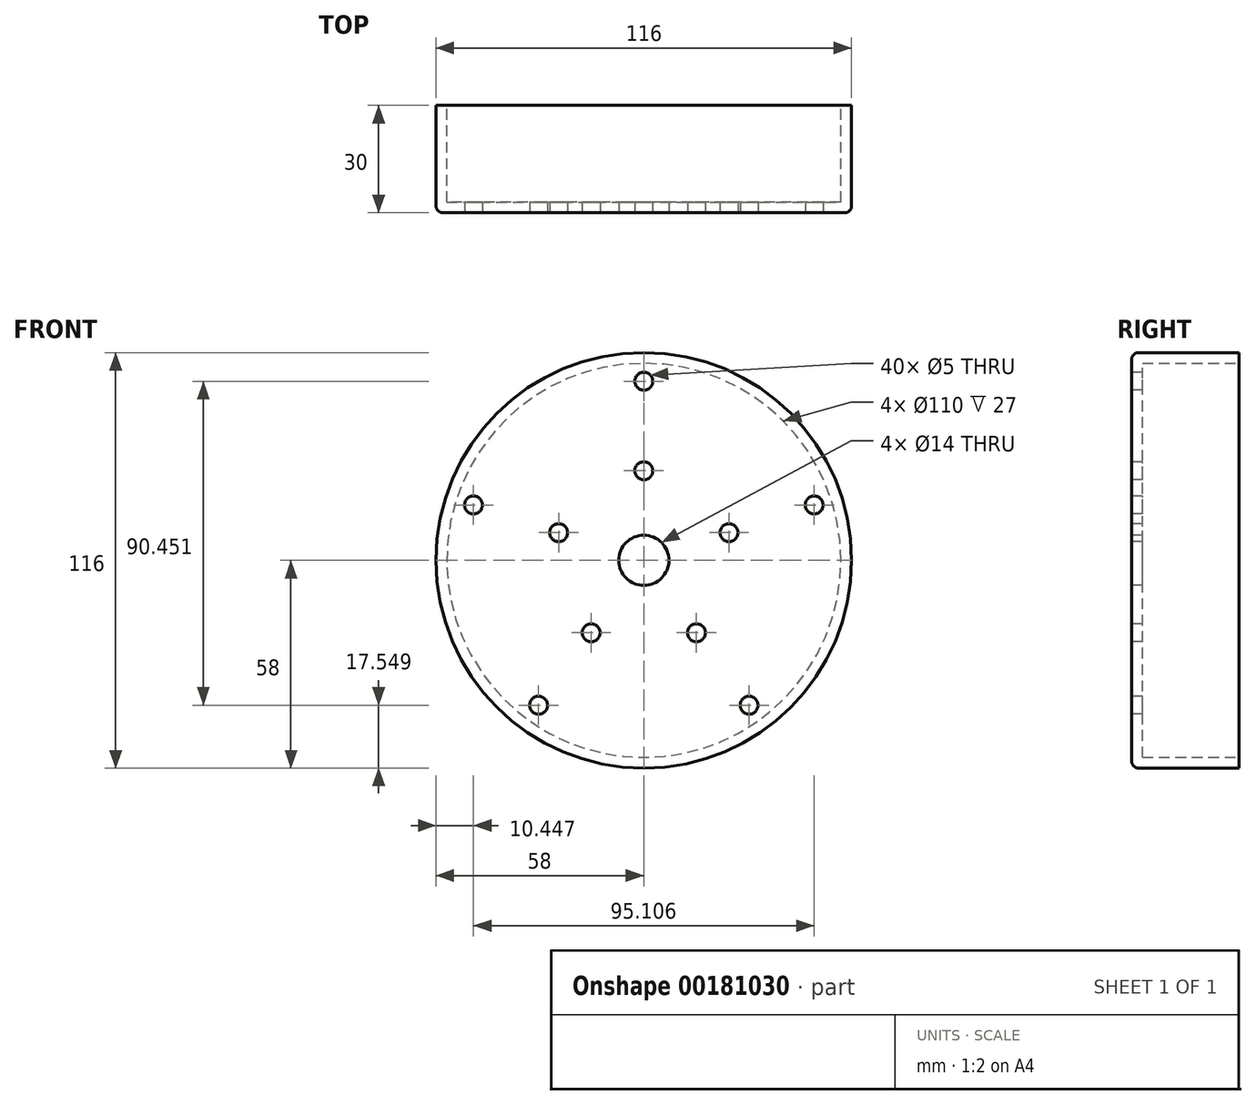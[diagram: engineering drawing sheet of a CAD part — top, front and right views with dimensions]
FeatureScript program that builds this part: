
annotation { "Feature Type Name" : "Feature", "Feature Type Description" : "" }
export const myFeature = defineFeature(function(context is Context, id is Id, definition is map)
    precondition{}
    {
        {
            var Q0;
            Q0=qCreatedBy(makeId("Front.planeOp"),FACE);
            var sketch = newSketch(context, id + "F0", { "sketchPlane" : qUnion([Q0])});
            skCircle(sketch, "E0", {"center": v(0, 0) * mm, "radius": 58 * mm});
            skSolve(sketch);
        }
        {
            var Q0;
            Q0=qSketchRegion(id+"F0",true);
            extrude(context, id + "F1", {"entities" : qUnion([Q0]), "depth" : 30 * mm});
        }
        {
            var Q0;
            Q0=makeQuery(id+"F1.opExtrude","CAP_FACE",FACE,{"disambiguationData":[OSD([sQuery(id+"F0.wireOp",EDGE,"E0")])],"isStart":true});
            shell(context, id + "F2", {"entities" : qUnion([Q0]), "thickness" : 3 * mm});
        }
        {
            var Q0;
            Q0=makeQuery(id+"F1.opExtrude","CAP_EDGE",EDGE,{"disambiguationData":[OSD([sQuery(id+"F0.wireOp",EDGE,"E0")])],"isStart":false});
            fillet(context, id + "F3", {"entities" : qUnion([Q0]), "radius" : 2 * mm, "tangentPropagation" : true, "allowEdgeOverflow" : false});
        }
        {
            var Q0;
            Q0=makeQuery(id+"F1.opExtrude","CAP_FACE",FACE,{"disambiguationData":[OSD([sQuery(id+"F0.wireOp",EDGE,"E0")])],"isStart":false});
            var sketch = newSketch(context, id + "F4", { "sketchPlane" : qUnion([Q0])});
            skPoint(sketch, "E1", {"position": v(0, 0) * mm});
            skSolve(sketch);
        }
        {
            var Q0;
            Q0=sQuery(id+"F4.wireOp",VERTEX,"E1");
            var Q1;
            Q1=makeQuery(id+"F1.opExtrude","SWEPT_BODY",BODY,{"disambiguationData":[OSD([sQuery(id+"F0.wireOp",EDGE,"E0")])]});
            hole(context, id + "F5", {"style" : HoleStyle.SIMPLE, "endStyle" : HoleEndStyle.THROUGH, "holeDiameter" : 14 * mm, "locations" : qUnion([Q0]), "scope" : qUnion([Q1]), "isTappedThrough" : true});
        }
        {
            var Q0;
            Q0=makeQuery(id+"F1.opExtrude","CAP_FACE",FACE,{"disambiguationData":[OSD([sQuery(id+"F0.wireOp",EDGE,"E0")])],"isStart":false});
            var sketch = newSketch(context, id + "F6", { "sketchPlane" : qUnion([Q0])});
            skPoint(sketch, "E2", {"position": v(0, 25) * mm});
            skPoint(sketch, "E3", {"position": v(0, 50) * mm});
            skPoint(sketch, "E4.1.0", {"position": v(-47.55, 15.45) * mm});
            skPoint(sketch, "E4.1.1", {"position": v(-23.78, 7.73) * mm});
            skPoint(sketch, "E4.2.0", {"position": v(-29.39, -40.45) * mm});
            skPoint(sketch, "E4.2.1", {"position": v(-14.7, -20.23) * mm});
            skPoint(sketch, "E4.3.0", {"position": v(29.39, -40.45) * mm});
            skPoint(sketch, "E4.3.1", {"position": v(14.7, -20.23) * mm});
            skPoint(sketch, "E4.4.0", {"position": v(47.55, 15.45) * mm});
            skPoint(sketch, "E4.4.1", {"position": v(23.78, 7.73) * mm});
            skPoint(sketch, "E4.center", {"position": v(0, 0) * mm});
            skSolve(sketch);
        }
        {
            var Q0;
            Q0=sQuery(id+"F6.wireOp",VERTEX,"E2");
            var Q1;
            Q1=sQuery(id+"F6.wireOp",VERTEX,"E3");
            var Q2;
            Q2=sQuery(id+"F6.wireOp",VERTEX,"E4.1.1");
            var Q3;
            Q3=sQuery(id+"F6.wireOp",VERTEX,"E4.1.0");
            var Q4;
            Q4=sQuery(id+"F6.wireOp",VERTEX,"E4.2.0");
            var Q5;
            Q5=sQuery(id+"F6.wireOp",VERTEX,"E4.2.1");
            var Q6;
            Q6=sQuery(id+"F6.wireOp",VERTEX,"E4.3.1");
            var Q7;
            Q7=sQuery(id+"F6.wireOp",VERTEX,"E4.3.0");
            var Q8;
            Q8=sQuery(id+"F6.wireOp",VERTEX,"E4.4.1");
            var Q9;
            Q9=sQuery(id+"F6.wireOp",VERTEX,"E4.4.0");
            var Q10;
            Q10=makeQuery(id+"F1.opExtrude","SWEPT_BODY",BODY,{"disambiguationData":[OSD([sQuery(id+"F0.wireOp",EDGE,"E0")])]});
            hole(context, id + "F7", {"style" : HoleStyle.SIMPLE, "endStyle" : HoleEndStyle.THROUGH, "holeDiameter" : 5 * mm, "locations" : qUnion([Q0, Q1, Q2, Q3, Q4, Q5, Q6, Q7, Q8, Q9]), "scope" : qUnion([Q10]), "isTappedThrough" : true});
        }
    });
